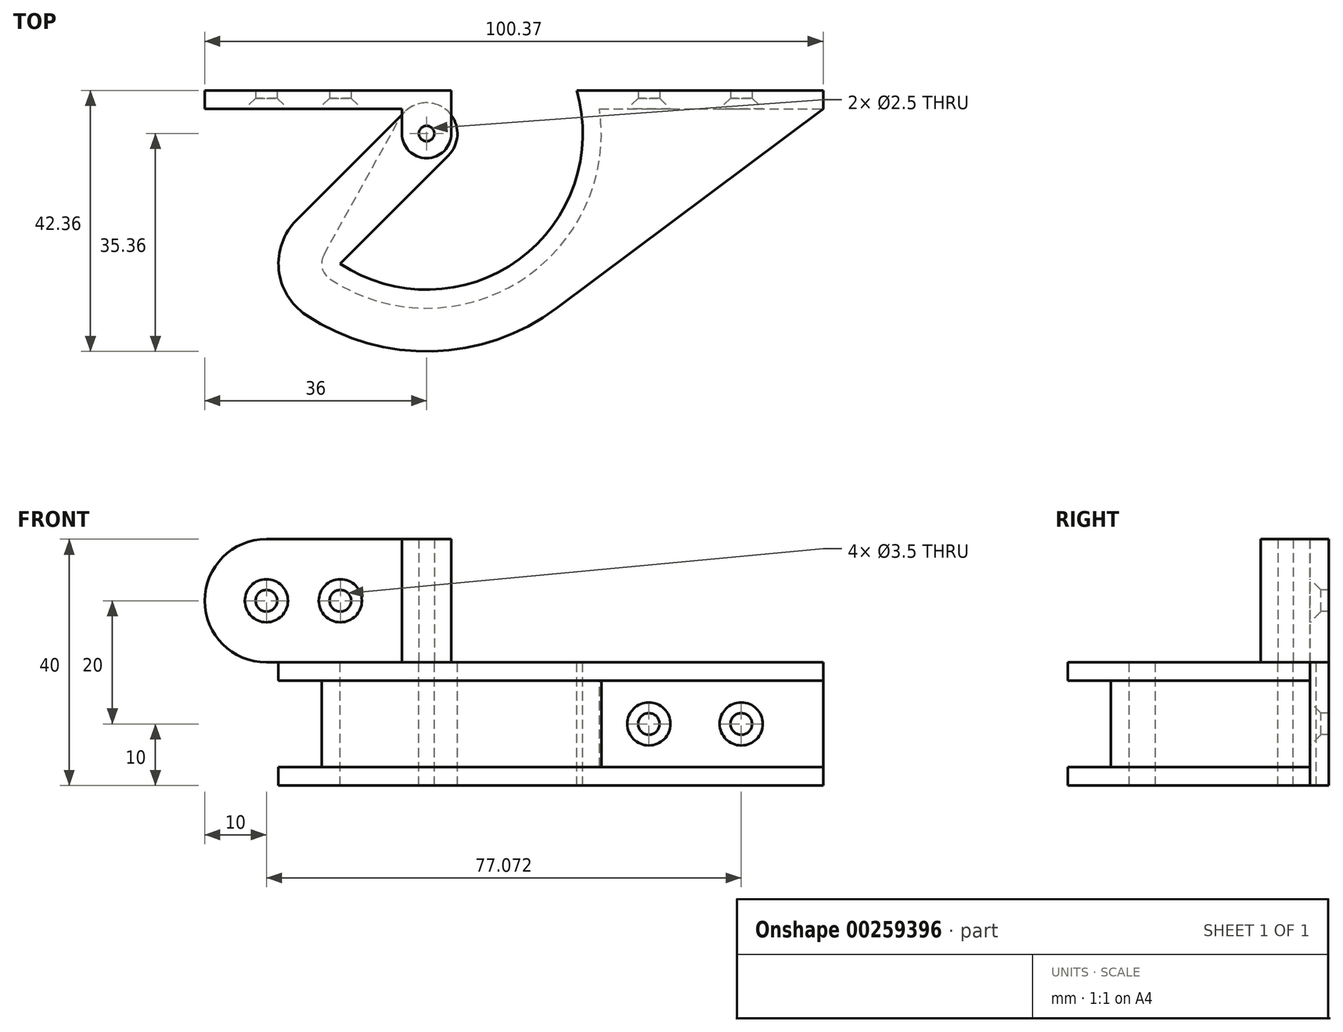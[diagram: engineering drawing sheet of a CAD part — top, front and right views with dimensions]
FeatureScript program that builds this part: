
annotation { "Feature Type Name" : "Feature", "Feature Type Description" : "" }
export const myFeature = defineFeature(function(context is Context, id is Id, definition is map)
    precondition{}
    {
        {
            var Q0;
            Q0=qCreatedBy(makeId("Top.planeOp"),FACE);
            var sketch = newSketch(context, id + "F0", { "sketchPlane" : qUnion([Q0])});
            skLineSegment(sketch, "E0.bottom", {"start": v(-36, 7) * mm, "end": v(4, 7) * mm});
            skLineSegment(sketch, "E0.top", {"start": v(-36, 4) * mm, "end": v(-4, 4) * mm});
            skLineSegment(sketch, "E0.left", {"start": v(-36, 7) * mm, "end": v(-36, 4) * mm});
            skLineSegment(sketch, "E0.right", {"start": v(4, 7) * mm, "end": v(4, 0) * mm});
            skArc(sketch, "E1", {"start": v(-4, 0) * mm, "mid": v(0, -4) * mm, "end": v(4, 0) * mm});
            skLineSegment(sketch, "E2", {"start": v(-4, 0) * mm, "end": v(-4, 4) * mm});
            skLineSegment(sketch, "E3", {"start": v(0, 7) * mm, "end": v(0, -3) * mm, "construction": true});
            skCircle(sketch, "E4.converted", {"center": v(0, 0) * mm, "radius": 1.25 * mm});
            skSolve(sketch);
        }
        {
            var Q0;
            Q0=qCreatedBy(makeId("Top.planeOp"),FACE);
            var sketch = newSketch(context, id + "F1", { "sketchPlane" : qUnion([Q0])});
            skLineSegment(sketch, "E5.0.4", {"start": v(4, 0) * mm, "end": v(4, 7) * mm, "construction": true});
            skLineSegment(sketch, "E5.0.5", {"start": v(4, 7) * mm, "end": v(-36, 7) * mm, "construction": true});
            skLineSegment(sketch, "E5.0.6", {"start": v(-36, 7) * mm, "end": v(-36, 4) * mm, "construction": true});
            skLineSegment(sketch, "E5.0.7", {"start": v(-36, 4) * mm, "end": v(-4, 4) * mm, "construction": true});
            skLineSegment(sketch, "E5.0.8", {"start": v(-4, 4) * mm, "end": v(-4, 0) * mm, "construction": true});
            skArc(sketch, "E5.0.9", {"start": v(-4, 0) * mm, "mid": v(0, -4) * mm, "end": v(4, 0) * mm, "construction": true});
            skArc(sketch, "E6", {"start": v(3.54, -3.54) * mm, "mid": v(3.01, 4) * mm, "end": v(-4.37, 2.43) * mm});
            skLineSegment(sketch, "E7", {"start": v(0, 0) * mm, "end": v(-25, -25) * mm, "construction": true});
            skLineSegment(sketch, "E8", {"start": v(-3.54, 3.54) * mm, "end": v(-28.28, -21.21) * mm});
            skArc(sketch, "E9", {"start": v(-28.28, -21.21) * mm, "mid": v(-5.02, -35) * mm, "end": v(21.18, -28.31) * mm});
            skLineSegment(sketch, "E10", {"start": v(3.54, -3.54) * mm, "end": v(-14.04, -21.11) * mm});
            skArc(sketch, "E11", {"start": v(-14.04, -21.11) * mm, "mid": v(14.97, -20.46) * mm, "end": v(24.37, 7) * mm});
            skLineSegment(sketch, "E12", {"start": v(4, 7) * mm, "end": v(18.81, 7) * mm, "construction": true});
            skLineSegment(sketch, "E13", {"start": v(18.81, 7) * mm, "end": v(18.81, 17) * mm, "construction": true});
            skLineSegment(sketch, "E14", {"start": v(18.81, 17) * mm, "end": v(-40.85, 17) * mm, "construction": true});
            skArc(sketch, "E15", {"start": v(24.37, 7) * mm, "mid": v(5.72, 24.7) * mm, "end": v(-18.81, 17) * mm, "construction": true});
            skArc(sketch, "E16", {"start": v(21.18, -28.31) * mm, "mid": v(23.18, 26.7) * mm, "end": v(-31, 17) * mm, "construction": true});
            skLineSegment(sketch, "E17", {"start": v(24.37, 7) * mm, "end": v(64.37, 7) * mm});
            skLineSegment(sketch, "E18", {"start": v(64.37, 4) * mm, "end": v(21.18, -28.31) * mm});
            skLineSegment(sketch, "E19", {"start": v(24.37, 7) * mm, "end": v(24.37, 17) * mm, "construction": true});
            skLineSegment(sketch, "E20", {"start": v(24.37, 17) * mm, "end": v(68.46, 17) * mm, "construction": true});
            skCircle(sketch, "E21.0", {"center": v(0, 0) * mm, "radius": 1.25 * mm});
            skLineSegment(sketch, "E22", {"start": v(64.37, 7) * mm, "end": v(64.37, 4) * mm});
            skLineSegment(sketch, "E23.0", {"start": v(28.07, 4) * mm, "end": v(64.37, 4) * mm});
            skArc(sketch, "E23.1", {"start": v(-17.94, -21.96) * mm, "mid": v(13.93, -24.7) * mm, "end": v(28.07, 4) * mm});
            skLineSegment(sketch, "E24", {"start": v(-17.94, -21.96) * mm, "end": v(-4.37, 2.43) * mm});
            skSolve(sketch);
        }
        {
            var Q0;
            Q0 = qSketchRegion(id + "F0", true);
            extrude(context, id + "F2", {"entities" : qUnion([Q0]), "depth" : 20 * mm});
        }
        {
            var Q0;
            {var subQ1=sQuery(id+"F1.wireOp",EDGE,"E10");Q0=makeQuery(id+"F1.imprint","IMPRINT",FACE,{"disambiguationData":[TD([[makeQuery(id+"F1.imprint","IMPRINT",EDGE,{"derivedFrom":subQ1}),-1.0]])]});}
            var Q1;
            {var subQ3=sQuery(id+"F1.wireOp",EDGE,"E8");Q1=makeQuery(id+"F1.imprint","IMPRINT",FACE,{"disambiguationData":[TD([[makeQuery(id+"F1.imprint","IMPRINT",EDGE,{"derivedFrom":subQ3}),1.0]])]});}
            extrude(context, id + "F3", {"entities" : qUnion([Q0, Q1]), "oppositeDirection" : true, "depth" : 20 * mm});
        }
        {
            var Q0;
            {var subQ3=sQuery(id+"F1.wireOp",EDGE,"E8");Q0=makeQuery(id+"F1.imprint","IMPRINT",FACE,{"disambiguationData":[TD([[makeQuery(id+"F1.imprint","IMPRINT",EDGE,{"derivedFrom":subQ3}),1.0]])]});}
            extrude(context, id + "F4", {"entities" : qUnion([Q0]), "operationType" : NewBodyOperationType.REMOVE, "oppositeDirection" : true, "depth" : 17 * mm, "hasSecondDirection" : true, "secondDirectionOppositeDirection" : true, "secondDirectionDepth" : 3 * mm});
        }
        {
            var Q0;
            Q0=makeQuery(id+"F2.opExtrude","CAP_EDGE",EDGE,{"disambiguationData":[OSD([sQuery(id+"F0.wireOp",EDGE,"E0.left")])],"isStart":false});
            var Q1;
            Q1=makeQuery(id+"F2.opExtrude","CAP_EDGE",EDGE,{"disambiguationData":[OSD([sQuery(id+"F0.wireOp",EDGE,"E0.left")])],"isStart":true});
            var Q2;
            {var subQ0=sQuery(id+"F1.wireOp",EDGE,"E21.0");var subQ1=sQuery(id+"F1.wireOp",EDGE,"E18");var subQ2=sQuery(id+"F1.wireOp",EDGE,"E9");var subQ3=sQuery(id+"F1.wireOp",EDGE,"E8");var subQ4=sQuery(id+"F1.wireOp",EDGE,"E6");Q2=makeQuery(id+"F4.boolean.opBoolean","SPLIT",EDGE,{"disambiguationData":[TD([makeQuery(id+"F4.opExtrude","CAP_FACE",FACE,{"disambiguationData":[OSD([subQ4,subQ3,subQ2,subQ1,subQ0,sQuery(id+"F1.wireOp",EDGE,"363b1121-1314-4e87-a7d9-f08991e2a48b.0"),sQuery(id+"F1.wireOp",EDGE,"363b1121-1314-4e87-a7d9-f08991e2a48b.1"),sQuery(id+"F1.wireOp",EDGE,"363b1121-1314-4e87-a7d9-f08991e2a48b.2")])],"isStart":true})])],"derivedFrom":makeQuery(id+"F3.opExtrude","SWEPT_EDGE",EDGE,{"disambiguationData":[OSD([subQ3,subQ2])]})});}
            var Q3;
            {var subQ0=sQuery(id+"F1.wireOp",EDGE,"E21.0");var subQ1=sQuery(id+"F1.wireOp",EDGE,"E18");var subQ2=sQuery(id+"F1.wireOp",EDGE,"E9");var subQ3=sQuery(id+"F1.wireOp",EDGE,"E8");var subQ4=sQuery(id+"F1.wireOp",EDGE,"E6");Q3=makeQuery(id+"F4.boolean.opBoolean","SPLIT",EDGE,{"disambiguationData":[TD([makeQuery(id+"F4.opExtrude","CAP_FACE",FACE,{"disambiguationData":[OSD([subQ4,subQ3,subQ2,subQ1,subQ0,sQuery(id+"F1.wireOp",EDGE,"363b1121-1314-4e87-a7d9-f08991e2a48b.0"),sQuery(id+"F1.wireOp",EDGE,"363b1121-1314-4e87-a7d9-f08991e2a48b.1"),sQuery(id+"F1.wireOp",EDGE,"363b1121-1314-4e87-a7d9-f08991e2a48b.2")])],"isStart":false})])],"derivedFrom":makeQuery(id+"F3.opExtrude","SWEPT_EDGE",EDGE,{"disambiguationData":[OSD([subQ3,subQ2])]})});}
            fillet(context, id + "F5", {"entities" : qUnion([Q0, Q1, Q2, Q3]), "radius" : 10 * mm, "tangentPropagation" : true, "allowEdgeOverflow" : false});
        }
        {
            var Q0;
            Q0=makeQuery(id+"F4.boolean.opBoolean","COPY",EDGE,{"derivedFrom":makeQuery(id+"F4.opExtrude","SWEPT_EDGE",EDGE,{"disambiguationData":[OSD([sQuery(id+"F1.wireOp",EDGE,"E23.1"),sQuery(id+"F1.wireOp",EDGE,"E24")])]})});
            fillet(context, id + "F6", {"entities" : qUnion([Q0]), "radius" : 3 * mm, "tangentPropagation" : true, "allowEdgeOverflow" : false});
        }
        {
            var Q0;
            Q0=makeQuery(id+"F4.boolean.opBoolean","COPY",FACE,{"derivedFrom":makeQuery(id+"F4.opExtrude","SWEPT_FACE",FACE,{"disambiguationData":[OSD([sQuery(id+"F1.wireOp",EDGE,"E23.0")])]})});
            var sketch = newSketch(context, id + "F7", { "sketchPlane" : qUnion([Q0])});
            skLineSegment(sketch, "E25.0", {"start": v(28.07, -17) * mm, "end": v(28.07, -3) * mm, "construction": true});
            skLineSegment(sketch, "E25.1", {"start": v(64.37, -17) * mm, "end": v(64.37, -3) * mm, "construction": true});
            skLineSegment(sketch, "E25.2", {"start": v(28.07, -17) * mm, "end": v(64.37, -17) * mm, "construction": true});
            skLineSegment(sketch, "E25.3", {"start": v(28.07, -3) * mm, "end": v(64.37, -3) * mm, "construction": true});
            skLineSegment(sketch, "E25.4", {"start": v(-26, 20) * mm, "end": v(-4, 20) * mm, "construction": true});
            skArc(sketch, "E25.5", {"start": v(-26, 20) * mm, "mid": v(-36, 10) * mm, "end": v(-26, 0) * mm, "construction": true});
            skLineSegment(sketch, "E25.6", {"start": v(-26, 0) * mm, "end": v(-4, 0) * mm, "construction": true});
            skLineSegment(sketch, "E25.7", {"start": v(-4, 20) * mm, "end": v(-4, 0) * mm, "construction": true});
            skPoint(sketch, "E26", {"position": v(-14, 10) * mm});
            skPoint(sketch, "E27", {"position": v(51.07, -10) * mm});
            skPoint(sketch, "E27.positionSnap0", {"position": v(64.37, -10) * mm});
            skPoint(sketch, "E28", {"position": v(36.07, -10) * mm});
            skSolve(sketch);
        }
        {
            var Q0;
            Q0=sQuery(id+"F7.wireOp",VERTEX,"E25.5.center");
            var Q1;
            Q1=sQuery(id+"F7.wireOp",VERTEX,"E26");
            var Q2;
            Q2=sQuery(id+"F7.wireOp",VERTEX,"E28");
            var Q3;
            Q3=sQuery(id+"F7.wireOp",VERTEX,"E27");
            var Q4;
            Q4=makeQuery(id+"F3.opExtrude","SWEPT_BODY",BODY,{"disambiguationData":[OSD([sQuery(id+"F1.wireOp",EDGE,"E6"),sQuery(id+"F1.wireOp",EDGE,"E8"),sQuery(id+"F1.wireOp",EDGE,"E9"),sQuery(id+"F1.wireOp",EDGE,"E10"),sQuery(id+"F1.wireOp",EDGE,"E11"),sQuery(id+"F1.wireOp",EDGE,"E17"),sQuery(id+"F1.wireOp",EDGE,"E18"),sQuery(id+"F1.wireOp",EDGE,"E21.0"),sQuery(id+"F1.wireOp",EDGE,"E22")])]});
            var Q5;
            Q5=makeQuery(id+"F2.opExtrude","SWEPT_BODY",BODY,{"disambiguationData":[OSD([sQuery(id+"F0.wireOp",EDGE,"E0.bottom"),sQuery(id+"F0.wireOp",EDGE,"E0.top"),sQuery(id+"F0.wireOp",EDGE,"E0.left"),sQuery(id+"F0.wireOp",EDGE,"E0.right"),sQuery(id+"F0.wireOp",EDGE,"E1"),sQuery(id+"F0.wireOp",EDGE,"E2"),sQuery(id+"F0.wireOp",EDGE,"E4.converted")])]});
            hole(context, id + "F8", {"style" : HoleStyle.C_SINK, "endStyle" : HoleEndStyle.BLIND, "holeDiameter" : 3.5 * mm, "cSinkDiameter" : 7 * mm, "cSinkAngle" : 90 * degree, "holeDepth" : 20 * mm, "tappedDepth" : 12 * mm, "tapClearance" : 3, "startFromSketch" : true, "locations" : qUnion([Q0, Q1, Q2, Q3]), "scope" : qUnion([Q4, Q5])});
        }
    });
